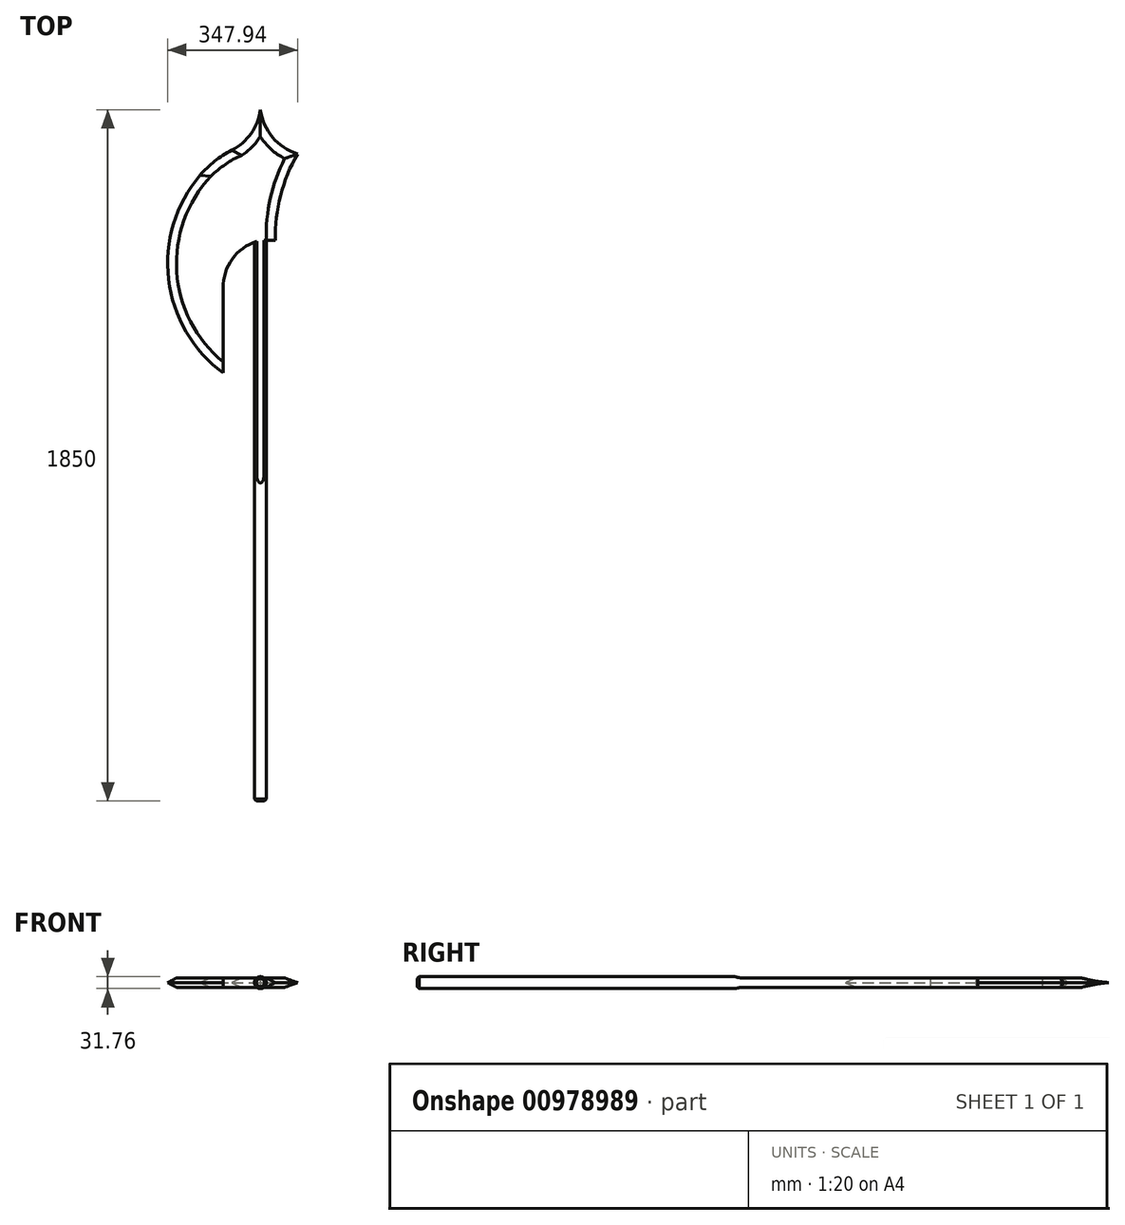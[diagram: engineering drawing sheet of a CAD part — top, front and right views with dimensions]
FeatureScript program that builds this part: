
annotation { "Feature Type Name" : "Feature", "Feature Type Description" : "" }
export const myFeature = defineFeature(function(context is Context, id is Id, definition is map)
    precondition{}
    {
        {
            var Q0;
            Q0=qCreatedBy(makeId("Front.planeOp"),FACE);
            var sketch = newSketch(context, id + "F0", { "sketchPlane" : qUnion([Q0])});
            skCircle(sketch, "E0", {"center": v(0, 0) * mm, "radius": 15.88 * mm});
            skSolve(sketch);
        }
        {
            var Q0;
            Q0 = qSketchRegion(id + "F0", true);
            extrude(context, id + "F1", {"entities" : qUnion([Q0]), "depth" : 1600 * mm, "offsetDistance" : 25 * mm});
        }
        {
            var Q0;
            Q0=qCreatedBy(makeId("Top.planeOp"),FACE);
            var sketch = newSketch(context, id + "F2", { "sketchPlane" : qUnion([Q0])});
            skArc(sketch, "E1", {"start": v(-99.66, 131.97) * mm, "mid": v(-248.28, -161.29) * mm, "end": v(-99.66, -454.55) * mm});
            skLineSegment(sketch, "E2", {"start": v(0, 0) * mm, "end": v(0, 250) * mm});
            skArc(sketch, "E3", {"start": v(-99.66, 131.97) * mm, "mid": v(-32.32, 176.2) * mm, "end": v(0, 250) * mm});
            skLineSegment(sketch, "E4", {"start": v(-99.66, -454.55) * mm, "end": v(-99.66, 0) * mm});
            skLineSegment(sketch, "E5", {"start": v(0, 0) * mm, "end": v(0, -100) * mm});
            skArc(sketch, "E6", {"start": v(0, -100) * mm, "mid": v(-72.33, -146.02) * mm, "end": v(-99.66, -227.27) * mm});
            skLineSegment(sketch, "E7", {"start": v(-99.66, 131.97) * mm, "end": v(0, 0) * mm});
            skArc(sketch, "E8.MirrorCS", {"start": v(99.66, 131.97) * mm, "mid": v(32.32, 176.2) * mm, "end": v(0, 250) * mm});
            skLineSegment(sketch, "E9", {"start": v(0, -100) * mm, "end": v(40, -100) * mm});
            skArc(sketch, "E10", {"start": v(99.66, 131.97) * mm, "mid": v(53.8, 20.1) * mm, "end": v(40, -100) * mm});
            skSolve(sketch);
        }
        {
            var Q0;
            {var subQ4=sQuery(id+"F2.wireOp",EDGE,"E1");Q0=makeQuery(id+"F2.imprint","IMPRINT",FACE,{"disambiguationData":[TD([[makeQuery(id+"F2.imprint","IMPRINT",EDGE,{"derivedFrom":subQ4}),1.0]])]});}
            var Q1;
            Q1=makeQuery(id+"F2.imprint","IMPRINT",FACE,{"disambiguationData":[TD([[makeQuery(id+"F2.imprint","IMPRINT",EDGE,{"derivedFrom":sQuery(id+"F2.wireOp",EDGE,"E2")}),1.0]])]});
            var Q2;
            Q2=makeQuery(id+"F2.imprint","IMPRINT",FACE,{"disambiguationData":[TD([[makeQuery(id+"F2.imprint","IMPRINT",EDGE,{"derivedFrom":sQuery(id+"F2.wireOp",EDGE,"E2")}),-1.0]])]});
            extrude(context, id + "F3", {"entities" : qUnion([Q0, Q1, Q2]), "operationType" : NewBodyOperationType.ADD, "depth" : 12.5 * mm, "offsetDistance" : 25 * mm, "hasSecondDirection" : true, "secondDirectionOppositeDirection" : true, "secondDirectionDepth" : 12.5 * mm});
        }
        {
            var Q0;
            Q0=makeQuery(id+"F3.opExtrude","SWEPT_EDGE",EDGE,{"disambiguationData":[OSD([sQuery(id+"F2.wireOp",EDGE,"E1"),sQuery(id+"F2.wireOp",EDGE,"E3"),sQuery(id+"F2.wireOp",EDGE,"E7")])]});
            fillet(context, id + "F4", {"entities" : qUnion([Q0]), "radius" : 273.67 * mm, "tangentPropagation" : true, "allowEdgeOverflow" : false});
        }
        {
            var Q0;
            Q0=makeQuery(id+"F3.opExtrude","SWEPT_FACE",FACE,{"disambiguationData":[OSD([sQuery(id+"F2.wireOp",EDGE,"E4")])]});
            var sketch = newSketch(context, id + "F5", { "sketchPlane" : qUnion([Q0])});
            skLineSegment(sketch, "E11", {"start": v(-454.55, 0) * mm, "end": v(-424.55, 0) * mm});
            skLineSegment(sketch, "E12", {"start": v(-424.55, 0) * mm, "end": v(-424.55, 12.5) * mm});
            skLineSegment(sketch, "E13", {"start": v(-424.55, 12.5) * mm, "end": v(-454.55, 0) * mm});
            skLineSegment(sketch, "E14", {"start": v(-454.55, 0) * mm, "end": v(-424.55, -12.5) * mm});
            skLineSegment(sketch, "E15", {"start": v(-424.55, -12.5) * mm, "end": v(-424.55, 0) * mm});
            skSolve(sketch);
        }
        {
            var Q0;
            {var subQ0=sQuery(id+"F5.wireOp",EDGE,"E13");Q0=makeQuery(id+"F5.imprint","IMPRINT",FACE,{"disambiguationData":[TD([[makeQuery(id+"F5.imprint","IMPRINT",EDGE,{"derivedFrom":subQ0}),-1.0]])]});}
            var Q1;
            {var subQ0=sQuery(id+"F5.wireOp",EDGE,"E14");Q1=makeQuery(id+"F5.imprint","IMPRINT",FACE,{"disambiguationData":[TD([[makeQuery(id+"F5.imprint","IMPRINT",EDGE,{"derivedFrom":subQ0}),-1.0]])]});}
            var Q2;
            {var subQ0=sQuery(id+"F2.wireOp",EDGE,"E3");var subQ1=sQuery(id+"F2.wireOp",EDGE,"E1");Q2=makeQuery(id+"F4.opFillet","BLEND_EDGE",EDGE,{"blendedFrom":[makeQuery(id+"F3.opExtrude","SWEPT_EDGE",EDGE,{"disambiguationData":[OSD([subQ1,subQ0,sQuery(id+"F2.wireOp",EDGE,"E7")])]}),makeQuery(id+"F3.opExtrude","CAP_FACE",FACE,{"disambiguationData":[OSD([subQ1,subQ0,sQuery(id+"F2.wireOp",EDGE,"E4"),sQuery(id+"F2.wireOp",EDGE,"E6"),sQuery(id+"F2.wireOp",EDGE,"E8.MirrorCS"),sQuery(id+"F2.wireOp",EDGE,"E9"),sQuery(id+"F2.wireOp",EDGE,"E10")])],"isStart":true})],"blendedInto":[makeQuery(id+"F3.opExtrude","CAP_FACE",FACE,{"disambiguationData":[OSD([subQ1,subQ0,sQuery(id+"F2.wireOp",EDGE,"E4"),sQuery(id+"F2.wireOp",EDGE,"E6"),sQuery(id+"F2.wireOp",EDGE,"E8.MirrorCS"),sQuery(id+"F2.wireOp",EDGE,"E9"),sQuery(id+"F2.wireOp",EDGE,"E10")])],"isStart":true})]});}
            var Q3;
            Q3=makeQuery(id+"F3.opExtrude","CAP_EDGE",EDGE,{"disambiguationData":[OSD([sQuery(id+"F2.wireOp",EDGE,"E1")])],"isStart":true});
            var Q4;
            Q4=makeQuery(id+"F3.opExtrude","CAP_EDGE",EDGE,{"disambiguationData":[OSD([sQuery(id+"F2.wireOp",EDGE,"E3")])],"isStart":true});
            var Q5;
            Q5=makeQuery(id+"F3.opExtrude","CAP_EDGE",EDGE,{"disambiguationData":[OSD([sQuery(id+"F2.wireOp",EDGE,"E8.MirrorCS")])],"isStart":true});
            var Q6;
            Q6=makeQuery(id+"F3.opExtrude","CAP_EDGE",EDGE,{"disambiguationData":[OSD([sQuery(id+"F2.wireOp",EDGE,"E10")])],"isStart":true});
            sweep(context, id + "F6", {"operationType" : NewBodyOperationType.REMOVE, "profiles" : qUnion([Q0, Q1]), "path" : qUnion([Q2, Q3, Q4, Q5, Q6])});
        }
        {
            var Q0;
            Q0=qCreatedBy(makeId("Right.planeOp"),FACE);
            var sketch = newSketch(context, id + "F7", { "sketchPlane" : qUnion([Q0])});
            skLineSegment(sketch, "E16", {"start": v(0, 0) * mm, "end": v(-800, 0) * mm});
            skLineSegment(sketch, "E17", {"start": v(0, 0) * mm, "end": v(0, 12.5) * mm});
            skLineSegment(sketch, "E18", {"start": v(0, 12.5) * mm, "end": v(-800, 12.5) * mm});
            skLineSegment(sketch, "E19", {"start": v(-800, 12.5) * mm, "end": v(-800, 0) * mm});
            skLineSegment(sketch, "E20.MirrorCS", {"start": v(0, 0) * mm, "end": v(0, -12.5) * mm});
            skLineSegment(sketch, "E21.MirrorCS", {"start": v(0, -12.5) * mm, "end": v(-800, -12.5) * mm});
            skLineSegment(sketch, "E22.MirrorCS", {"start": v(-800, -12.5) * mm, "end": v(-800, 0) * mm});
            skLineSegment(sketch, "E23", {"start": v(-800, 12.5) * mm, "end": v(-800, 46.46) * mm});
            skLineSegment(sketch, "E24", {"start": v(-800, 46.46) * mm, "end": v(0, 46.46) * mm});
            skLineSegment(sketch, "E25", {"start": v(0, 46.46) * mm, "end": v(0, 12.5) * mm});
            skLineSegment(sketch, "E26.MirrorCS", {"start": v(0, -46.46) * mm, "end": v(0, -12.5) * mm});
            skLineSegment(sketch, "E27.MirrorCS", {"start": v(-800, -46.46) * mm, "end": v(0, -46.46) * mm});
            skLineSegment(sketch, "E28.MirrorCS", {"start": v(-800, -12.5) * mm, "end": v(-800, -46.46) * mm});
            skSolve(sketch);
        }
        {
            var Q0;
            Q0=makeQuery(id+"F7.imprint","IMPRINT",FACE,{"disambiguationData":[TD([[makeQuery(id+"F7.imprint","IMPRINT",EDGE,{"derivedFrom":sQuery(id+"F7.wireOp",EDGE,"E18")}),-1.0]])]});
            var Q1;
            Q1=makeQuery(id+"F7.imprint","IMPRINT",FACE,{"disambiguationData":[TD([[makeQuery(id+"F7.imprint","IMPRINT",EDGE,{"derivedFrom":sQuery(id+"F7.wireOp",EDGE,"E21.MirrorCS")}),1.0]])]});
            extrude(context, id + "F8", {"entities" : qUnion([Q0, Q1]), "operationType" : NewBodyOperationType.REMOVE, "oppositeDirection" : true, "depth" : 462 * mm, "offsetDistance" : 25 * mm, "hasSecondDirection" : true, "secondDirectionOppositeDirection" : false, "secondDirectionDepth" : 376 * mm});
        }
        {
            var Q0;
            Q0=makeQuery(id+"F8.boolean.opBoolean","COPY",EDGE,{"derivedFrom":makeQuery(id+"F8.opExtrude","SWEPT_EDGE",EDGE,{"disambiguationData":[OSD([sQuery(id+"F7.wireOp",EDGE,"E18"),sQuery(id+"F7.wireOp",EDGE,"E19"),sQuery(id+"F7.wireOp",EDGE,"E23")])]})});
            var Q1;
            Q1=makeQuery(id+"F8.boolean.opBoolean","COPY",EDGE,{"derivedFrom":makeQuery(id+"F8.opExtrude","SWEPT_EDGE",EDGE,{"disambiguationData":[OSD([sQuery(id+"F7.wireOp",EDGE,"E21.MirrorCS"),sQuery(id+"F7.wireOp",EDGE,"E22.MirrorCS"),sQuery(id+"F7.wireOp",EDGE,"E28.MirrorCS")])]})});
            fillet(context, id + "F9", {"entities" : qUnion([Q0, Q1]), "radius" : 73.15 * mm, "tangentPropagation" : true, "allowEdgeOverflow" : false});
        }
        {
            var Q0;
            Q0=makeQuery(id+"F1.opExtrude","CAP_EDGE",EDGE,{"disambiguationData":[OSD([sQuery(id+"F0.wireOp",EDGE,"E0")])],"isStart":false});
            chamfer(context, id + "F10", {"entities" : qUnion([Q0]), "width" : 5 * mm, "tangentPropagation" : true});
        }
    });
